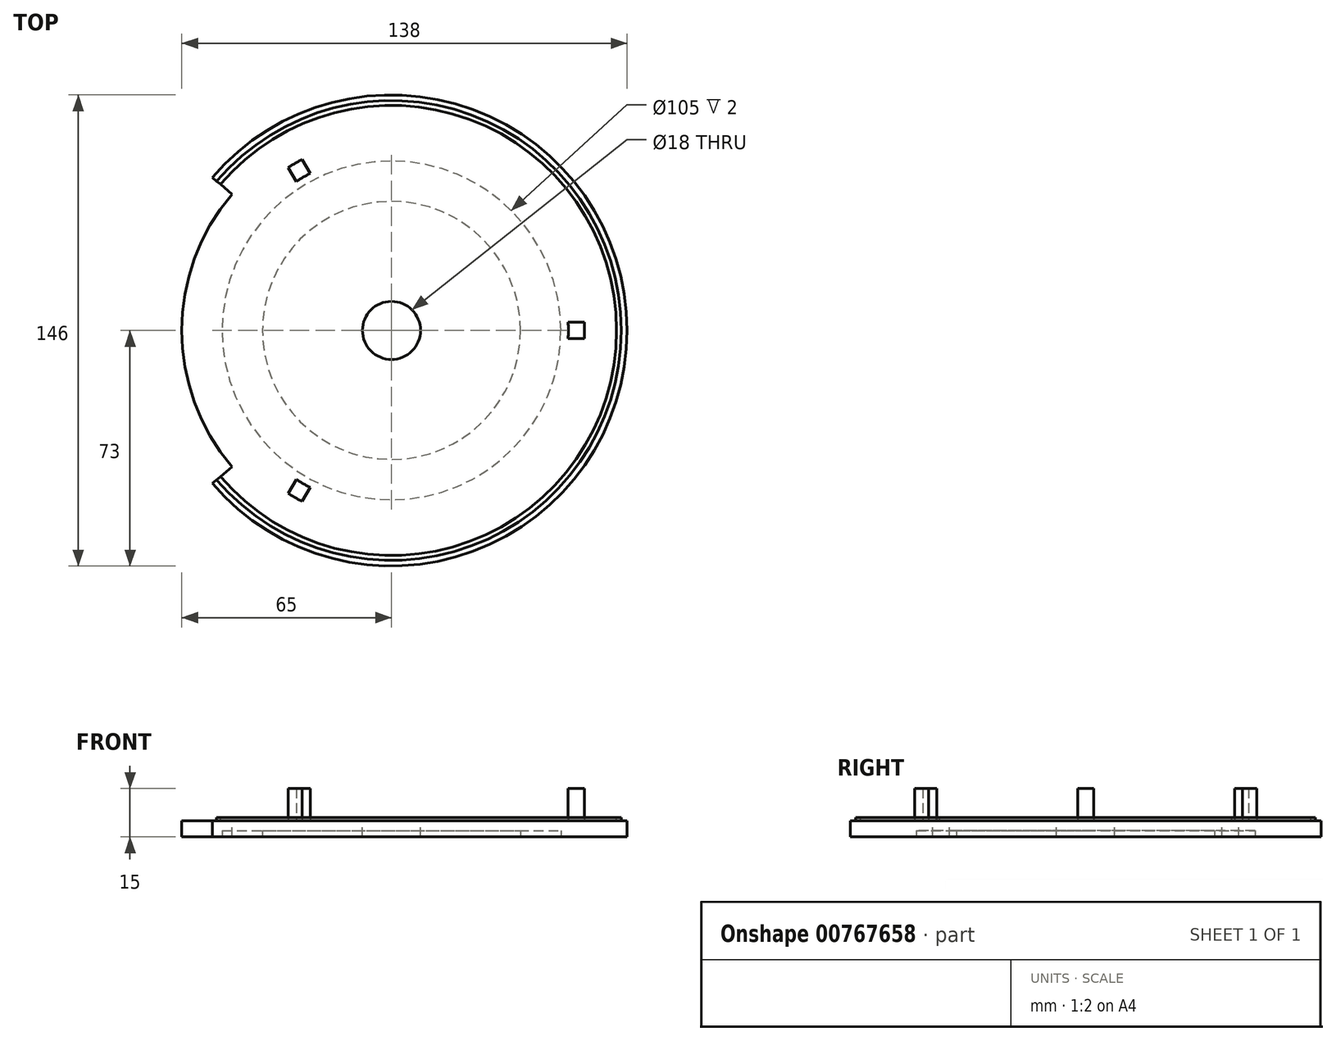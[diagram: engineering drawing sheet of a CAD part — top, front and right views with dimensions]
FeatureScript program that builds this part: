
annotation { "Feature Type Name" : "Feature", "Feature Type Description" : "" }
export const myFeature = defineFeature(function(context is Context, id is Id, definition is map)
    precondition{}
    {
        {
            var Q0;
            Q0=qCreatedBy(makeId("Front.planeOp"),FACE);
            var sketch = newSketch(context, id + "F0", { "sketchPlane" : qUnion([Q0])});
            skLineSegment(sketch, "E0", {"start": v(0, 0) * mm, "end": v(-73, 0) * mm});
            skLineSegment(sketch, "E1", {"start": v(-73, 0) * mm, "end": v(-73, 5) * mm});
            skLineSegment(sketch, "E2", {"start": v(-73, 5) * mm, "end": v(-71.25, 5) * mm});
            skLineSegment(sketch, "E3", {"start": v(-71.25, 6) * mm, "end": v(-71.25, 5) * mm});
            skLineSegment(sketch, "E4", {"start": v(-71.25, 6) * mm, "end": v(-69.75, 6) * mm});
            skLineSegment(sketch, "E5", {"start": v(-69.75, 5) * mm, "end": v(-69.75, 6) * mm});
            skLineSegment(sketch, "E6", {"start": v(-69.75, 5) * mm, "end": v(0, 5) * mm});
            skLineSegment(sketch, "E7", {"start": v(0, 5) * mm, "end": v(0, 0) * mm});
            skSolve(sketch);
        }
        {
            var Q0;
            Q0 = qSketchRegion(id + "F0", true);
            var Q1;
            Q1=sQuery(id+"F0.wireOp",EDGE,"E7");
            revolve(context, id + "F1", {"surfaceOperationType" : NewSurfaceOperationType.NEW, "entities" : qUnion([Q0]), "axis" : qUnion([Q1]), "revolveType" : RevolveType.FULL});
        }
        {
            var Q0;
            Q0=makeQuery(id+"F1.opRevolve","SWEPT_FACE",FACE,{"disambiguationData":[OSD([sQuery(id+"F0.wireOp",EDGE,"E0")])]});
            var sketch = newSketch(context, id + "F2", { "sketchPlane" : qUnion([Q0])});
            skCircle(sketch, "E8", {"center": v(0, 0) * mm, "radius": 40 * mm});
            skCircle(sketch, "E9", {"center": v(0, 0) * mm, "radius": 52.5 * mm});
            skSolve(sketch);
        }
        {
            var Q0;
            Q0 = qSketchRegion(id + "F2", true);
            extrude(context, id + "F3", {"entities" : qUnion([Q0]), "operationType" : NewBodyOperationType.REMOVE, "oppositeDirection" : true, "depth" : 2 * mm, "offsetDistance" : 25 * mm});
        }
        {
            var Q0;
            {var subQ0=sQuery(id+"Fp4Zue3Vz79XB9f_1.wireOp",EDGE,"VD89JmrG-62VO-vHXq-DP9O-YnilTvRGh6i4");var subQ1=makeQuery(id+"FPTM3FpEX4F2mh5_1.opExtrude","SWEPT_FACE",FACE,{"disambiguationData":[OSD([subQ0])]});Q0=makeQuery(id+"FLcIG0mrpST3dWv_1.boolean.opBoolean","MERGE",FACE,{"derivedFrom":[makeQuery(id+"FPTM3FpEX4F2mh5_1.boolean.opBoolean","SPLIT",FACE,{"disambiguationData":[TD([subQ1])],"derivedFrom":makeQuery(id+"F1.opRevolve","SWEPT_FACE",FACE,{"disambiguationData":[OSD([sQuery(id+"F0.wireOp",EDGE,"E2")])]})}),makeQuery(id+"FPTM3FpEX4F2mh5_1.boolean.opBoolean","SPLIT",FACE,{"disambiguationData":[TD([subQ1])],"derivedFrom":makeQuery(id+"F1.opRevolve","SWEPT_FACE",FACE,{"disambiguationData":[OSD([sQuery(id+"F0.wireOp",EDGE,"E6")])]})}),makeQuery(id+"FLcIG0mrpST3dWv_1.opExtrude","CAP_FACE",FACE,{"disambiguationData":[OSD([sQuery(id+"Fp4Zue3Vz79XB9f_1.wireOp",EDGE,"tnAMoaUn-WlWp-dVbr-L1dn-HdUlROP434XS"),sQuery(id+"Fp4Zue3Vz79XB9f_1.wireOp",EDGE,"Ka5YY56O-CeMJ-ficc-zg4t-y46oxInyd5XU"),subQ0,sQuery(id+"Fp4Zue3Vz79XB9f_1.wireOp",EDGE,"8F6t0DVd-bhsd-ujaL-enMg-pBpWDFIRCPrb.bottom"),sQuery(id+"Fp4Zue3Vz79XB9f_1.wireOp",EDGE,"8F6t0DVd-bhsd-ujaL-enMg-pBpWDFIRCPrb.top"),sQuery(id+"Fp4Zue3Vz79XB9f_1.wireOp",EDGE,"8F6t0DVd-bhsd-ujaL-enMg-pBpWDFIRCPrb.left"),sQuery(id+"Fp4Zue3Vz79XB9f_1.wireOp",EDGE,"8F6t0DVd-bhsd-ujaL-enMg-pBpWDFIRCPrb.right")])],"isStart":false})]});}
            var sketch = newSketch(context, id + "F4", { "sketchPlane" : qUnion([Q0])});
            skCircle(sketch, "E10", {"center": v(0, 0) * mm, "radius": 9 * mm});
            skSolve(sketch);
        }
        {
            var Q0;
            Q0 = qSketchRegion(id + "F4", true);
            var Q1;
            Q1=makeQuery(id+"F3.boolean.opBoolean","SPLIT",FACE,{"disambiguationData":[TD([makeQuery(id+"F3.opExtrude","SWEPT_FACE",FACE,{"disambiguationData":[OSD([sQuery(id+"F2.wireOp",EDGE,"E8")])]})])],"derivedFrom":makeQuery(id+"F1.opRevolve","SWEPT_FACE",FACE,{"disambiguationData":[OSD([sQuery(id+"F0.wireOp",EDGE,"E0")])]})});
            extrude(context, id + "F5", {"entities" : qUnion([Q0]), "operationType" : NewBodyOperationType.REMOVE, "endBound" : BoundingType.UP_TO_SURFACE, "oppositeDirection" : true, "depth" : 25 * mm, "endBoundEntityFace" : qUnion([Q1]), "offsetDistance" : 25 * mm});
        }
        {
            var Q0;
            Q0=makeQuery(id+"F1.opRevolve","SWEPT_FACE",FACE,{"disambiguationData":[OSD([sQuery(id+"F0.wireOp",EDGE,"E6")])]});
            var sketch = newSketch(context, id + "F6", { "sketchPlane" : qUnion([Q0])});
            skArc(sketch, "E11", {"start": v(59.75, 2.5) * mm, "mid": v(59.8, 0) * mm, "end": v(59.75, -2.5) * mm});
            skArc(sketch, "E12", {"start": v(54.75, 2.5) * mm, "mid": v(54.8, 0) * mm, "end": v(54.75, -2.5) * mm});
            skLineSegment(sketch, "E13", {"start": v(54.75, 2.5) * mm, "end": v(59.75, 2.5) * mm});
            skLineSegment(sketch, "E14", {"start": v(54.75, -2.5) * mm, "end": v(59.75, -2.5) * mm});
            skArc(sketch, "E15", {"start": v(54.75, 2.5) * mm, "mid": v(52.25, 0) * mm, "end": v(54.75, -2.5) * mm, "construction": true});
            skPoint(sketch, "E16", {"position": v(69.75, 0) * mm});
            skArc(sketch, "E17.1.0", {"start": v(-29.54, 46.16) * mm, "mid": v(-26.12, 45.25) * mm, "end": v(-25.2, 48.66) * mm, "construction": true});
            skLineSegment(sketch, "E17.1.1", {"start": v(-25.2, 48.66) * mm, "end": v(-27.7, 53) * mm});
            skLineSegment(sketch, "E17.1.2", {"start": v(-29.54, 46.16) * mm, "end": v(-32.04, 50.5) * mm});
            skArc(sketch, "E17.1.3", {"start": v(-29.54, 46.16) * mm, "mid": v(-27.4, 47.46) * mm, "end": v(-25.2, 48.66) * mm});
            skArc(sketch, "E17.1.4", {"start": v(-32.04, 50.5) * mm, "mid": v(-29.9, 51.8) * mm, "end": v(-27.7, 53) * mm});
            skArc(sketch, "E17.2.0", {"start": v(-25.2, -48.66) * mm, "mid": v(-26.12, -45.25) * mm, "end": v(-29.54, -46.16) * mm, "construction": true});
            skLineSegment(sketch, "E17.2.1", {"start": v(-29.54, -46.16) * mm, "end": v(-32.04, -50.5) * mm});
            skLineSegment(sketch, "E17.2.2", {"start": v(-25.2, -48.66) * mm, "end": v(-27.7, -53) * mm});
            skArc(sketch, "E17.2.3", {"start": v(-25.2, -48.66) * mm, "mid": v(-27.4, -47.46) * mm, "end": v(-29.54, -46.16) * mm});
            skArc(sketch, "E17.2.4", {"start": v(-27.7, -53) * mm, "mid": v(-29.9, -51.8) * mm, "end": v(-32.04, -50.5) * mm});
            skSolve(sketch);
        }
        {
            var Q0;
            Q0 = qSketchRegion(id + "F6", true);
            extrude(context, id + "F7", {"entities" : qUnion([Q0]), "operationType" : NewBodyOperationType.ADD, "depth" : 10 * mm, "offsetDistance" : 25 * mm});
        }
        {
            var Q0;
            Q0=makeQuery(id+"F1.opRevolve","SWEPT_FACE",FACE,{"disambiguationData":[OSD([sQuery(id+"F0.wireOp",EDGE,"E4")])]});
            var sketch = newSketch(context, id + "F8", { "sketchPlane" : qUnion([Q0])});
            skArc(sketch, "E18", {"start": v(-55.5, 47.4) * mm, "mid": v(-73, 0) * mm, "end": v(-55.5, -47.4) * mm});
            skArc(sketch, "E19", {"start": v(-49.43, 42.21) * mm, "mid": v(-65, 0) * mm, "end": v(-49.43, -42.21) * mm});
            skLineSegment(sketch, "E20", {"start": v(-55.5, 47.4) * mm, "end": v(-49.43, 42.21) * mm});
            skLineSegment(sketch, "E21", {"start": v(-55.5, -47.4) * mm, "end": v(-49.43, -42.21) * mm});
            skSolve(sketch);
        }
        {
            var Q0;
            Q0 = qSketchRegion(id + "F8", true);
            var Q1;
            Q1=makeQuery(id+"F3.boolean.opBoolean","SPLIT",FACE,{"disambiguationData":[TD([makeQuery(id+"F1.opRevolve","SWEPT_FACE",FACE,{"disambiguationData":[OSD([sQuery(id+"F0.wireOp",EDGE,"E1")])]})])],"derivedFrom":makeQuery(id+"F1.opRevolve","SWEPT_FACE",FACE,{"disambiguationData":[OSD([sQuery(id+"F0.wireOp",EDGE,"E0")])]})});
            extrude(context, id + "F9", {"entities" : qUnion([Q0]), "operationType" : NewBodyOperationType.REMOVE, "endBound" : BoundingType.UP_TO_SURFACE, "oppositeDirection" : true, "depth" : 25 * mm, "endBoundEntityFace" : qUnion([Q1]), "offsetDistance" : 25 * mm});
        }
    });
